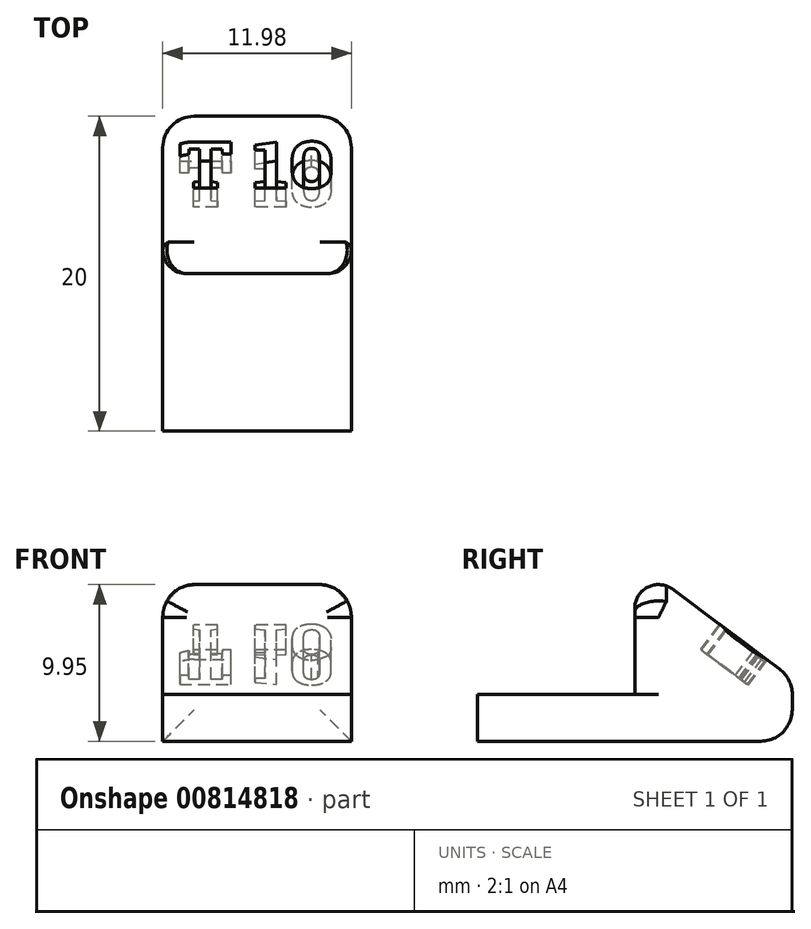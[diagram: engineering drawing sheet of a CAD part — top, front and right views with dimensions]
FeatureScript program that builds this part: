
annotation { "Feature Type Name" : "Feature", "Feature Type Description" : "" }
export const myFeature = defineFeature(function(context is Context, id is Id, definition is map)
    precondition{}
    {
        {
            var Q0;
            Q0=qCreatedBy(makeId("Top.planeOp"),FACE);
            var sketch = newSketch(context, id + "F0", { "sketchPlane" : qUnion([Q0])});
            skLineSegment(sketch, "E0.bottom", {"start": v(6, 10) * mm, "end": v(-5.99, 10) * mm});
            skLineSegment(sketch, "E0.top", {"start": v(6, -10) * mm, "end": v(-5.99, -10) * mm});
            skLineSegment(sketch, "E0.left", {"start": v(6, 10) * mm, "end": v(6, -10) * mm});
            skLineSegment(sketch, "E0.right", {"start": v(-5.99, 10) * mm, "end": v(-5.99, -10) * mm});
            skPoint(sketch, "E0.middle", {"position": v(0, 0) * mm});
            skSolve(sketch);
        }
        {
            var Q0;
            Q0 = qSketchRegion(id + "F0", true);
            extrude(context, id + "F1", {"entities" : qUnion([Q0]), "depth" : 2.98 * mm, "offsetDistance" : 25 * mm});
        }
        {
            var Q0;
            Q0=makeQuery(id+"F1.opExtrude","CAP_FACE",FACE,{"disambiguationData":[OSD([sQuery(id+"F0.wireOp",EDGE,"E0.bottom"),sQuery(id+"F0.wireOp",EDGE,"E0.top"),sQuery(id+"F0.wireOp",EDGE,"E0.left"),sQuery(id+"F0.wireOp",EDGE,"E0.right")])],"isStart":false});
            var sketch = newSketch(context, id + "F2", { "sketchPlane" : qUnion([Q0])});
            skLineSegment(sketch, "E1.bottom", {"start": v(-5.99, 10) * mm, "end": v(6, 10) * mm});
            skLineSegment(sketch, "E1.top", {"start": v(-5.99, 0) * mm, "end": v(6, 0) * mm});
            skLineSegment(sketch, "E1.left", {"start": v(-5.99, 10) * mm, "end": v(-5.99, 0) * mm});
            skLineSegment(sketch, "E1.right", {"start": v(6, 10) * mm, "end": v(6, 0) * mm});
            skSolve(sketch);
        }
        {
            var Q0;
            Q0=makeQuery(id+"F2.imprint","IMPRINT",FACE,{"disambiguationData":[TD([[makeQuery(id+"F2.imprint","IMPRINT",EDGE,{"derivedFrom":sQuery(id+"F2.wireOp",EDGE,"E1.bottom")}),1.0]])]});
            extrude(context, id + "F3", {"entities" : qUnion([Q0]), "operationType" : NewBodyOperationType.ADD, "depth" : 7 * mm, "offsetDistance" : 25 * mm});
        }
        {
            var Q0;
            Q0=makeQuery(id+"F3.opExtrude","CAP_EDGE",EDGE,{"disambiguationData":[OSD([sQuery(id+"F2.wireOp",EDGE,"E1.bottom")])],"isStart":false});
            chamfer(context, id + "F4", {"entities" : qUnion([Q0]), "chamferType" : ChamferType.TWO_OFFSETS, "width1" : 8 * mm, "oppositeDirection" : false, "width2" : 6 * mm, "tangentPropagation" : true});
        }
        {
            var Q0;
            Q0=makeQuery(id+"F4.opChamfer","BLEND_FACE",FACE,{"disambiguationData":[OSD([sQuery(id+"F2.wireOp",EDGE,"E1.bottom")])]});
            var sketch = newSketch(context, id + "F5", { "sketchPlane" : qUnion([Q0])});
            skText(sketch, "E2", { "text": "T 10", "fontName": "RobotoSlab-Bold.ttf"});
            const initialGuessF5  = {"E2": [-0.005, -8e-05, 1, 0, 0.0037]};
            skSetInitialGuess(sketch, initialGuessF5);
            skSolve(sketch);
        }
        {
            var Q0;
            Q0 = qSketchRegion(id + "F5", true);
            extrude(context, id + "F6", {"entities" : qUnion([Q0]), "operationType" : NewBodyOperationType.REMOVE, "oppositeDirection" : true, "depth" : 2 * mm, "offsetDistance" : 25 * mm});
        }
        {
            var Q0;
            {var subQ0=sQuery(id+"F2.wireOp",EDGE,"E1.bottom");Q0=makeQuery(id+"F4.opChamfer","BLEND_EDGE",EDGE,{"blendedFrom":[makeQuery(id+"F3.opExtrude","CAP_EDGE",EDGE,{"disambiguationData":[OSD([subQ0])],"isStart":false}),makeQuery(id+"F3.boolean.opBoolean","MERGE",FACE,{"derivedFrom":[makeQuery(id+"F1.opExtrude","SWEPT_FACE",FACE,{"disambiguationData":[OSD([sQuery(id+"F0.wireOp",EDGE,"E0.bottom")])]}),makeQuery(id+"F3.opExtrude","SWEPT_FACE",FACE,{"disambiguationData":[OSD([subQ0])]})]})],"blendedInto":[makeQuery(id+"F3.boolean.opBoolean","MERGE",FACE,{"derivedFrom":[makeQuery(id+"F1.opExtrude","SWEPT_FACE",FACE,{"disambiguationData":[OSD([sQuery(id+"F0.wireOp",EDGE,"E0.bottom")])]}),makeQuery(id+"F3.opExtrude","SWEPT_FACE",FACE,{"disambiguationData":[OSD([subQ0])]})]})]});}
            var Q1;
            {var subQ0=sQuery(id+"F2.wireOp",EDGE,"E1.bottom");Q1=makeQuery(id+"F4.opChamfer","BLEND_EDGE",EDGE,{"blendedFrom":[makeQuery(id+"F3.opExtrude","CAP_EDGE",EDGE,{"disambiguationData":[OSD([subQ0])],"isStart":false}),makeQuery(id+"F3.opExtrude","CAP_FACE",FACE,{"disambiguationData":[OSD([subQ0,sQuery(id+"F2.wireOp",EDGE,"E1.top"),sQuery(id+"F2.wireOp",EDGE,"E1.left"),sQuery(id+"F2.wireOp",EDGE,"E1.right")])],"isStart":false})],"blendedInto":[makeQuery(id+"F3.opExtrude","CAP_FACE",FACE,{"disambiguationData":[OSD([subQ0,sQuery(id+"F2.wireOp",EDGE,"E1.top"),sQuery(id+"F2.wireOp",EDGE,"E1.left"),sQuery(id+"F2.wireOp",EDGE,"E1.right")])],"isStart":false})]});}
            var Q2;
            Q2=makeQuery(id+"F4.opChamfer","BLEND_EDGE",EDGE,{"blendedFrom":[makeQuery(id+"F3.opExtrude","CAP_EDGE",EDGE,{"disambiguationData":[OSD([sQuery(id+"F2.wireOp",EDGE,"E1.bottom")])],"isStart":false}),makeQuery(id+"F3.boolean.opBoolean","MERGE",FACE,{"derivedFrom":[makeQuery(id+"F1.opExtrude","SWEPT_FACE",FACE,{"disambiguationData":[OSD([sQuery(id+"F0.wireOp",EDGE,"E0.left")])]}),makeQuery(id+"F3.opExtrude","SWEPT_FACE",FACE,{"disambiguationData":[OSD([sQuery(id+"F2.wireOp",EDGE,"E1.right")])]})]})],"blendedInto":[makeQuery(id+"F3.boolean.opBoolean","MERGE",FACE,{"derivedFrom":[makeQuery(id+"F1.opExtrude","SWEPT_FACE",FACE,{"disambiguationData":[OSD([sQuery(id+"F0.wireOp",EDGE,"E0.left")])]}),makeQuery(id+"F3.opExtrude","SWEPT_FACE",FACE,{"disambiguationData":[OSD([sQuery(id+"F2.wireOp",EDGE,"E1.right")])]})]})]});
            var Q3;
            Q3=makeQuery(id+"F4.opChamfer","BLEND_EDGE",EDGE,{"blendedFrom":[makeQuery(id+"F3.opExtrude","CAP_EDGE",EDGE,{"disambiguationData":[OSD([sQuery(id+"F2.wireOp",EDGE,"E1.bottom")])],"isStart":false}),makeQuery(id+"F3.boolean.opBoolean","MERGE",FACE,{"derivedFrom":[makeQuery(id+"F1.opExtrude","SWEPT_FACE",FACE,{"disambiguationData":[OSD([sQuery(id+"F0.wireOp",EDGE,"E0.right")])]}),makeQuery(id+"F3.opExtrude","SWEPT_FACE",FACE,{"disambiguationData":[OSD([sQuery(id+"F2.wireOp",EDGE,"E1.left")])]})]})],"blendedInto":[makeQuery(id+"F3.boolean.opBoolean","MERGE",FACE,{"derivedFrom":[makeQuery(id+"F1.opExtrude","SWEPT_FACE",FACE,{"disambiguationData":[OSD([sQuery(id+"F0.wireOp",EDGE,"E0.right")])]}),makeQuery(id+"F3.opExtrude","SWEPT_FACE",FACE,{"disambiguationData":[OSD([sQuery(id+"F2.wireOp",EDGE,"E1.left")])]})]})]});
            var Q4;
            Q4=makeQuery(id+"F3.boolean.opBoolean","MERGE",EDGE,{"derivedFrom":[makeQuery(id+"F1.opExtrude","SWEPT_EDGE",EDGE,{"disambiguationData":[OSD([sQuery(id+"F0.wireOp",EDGE,"E0.bottom"),sQuery(id+"F0.wireOp",EDGE,"E0.left")])]}),makeQuery(id+"F3.opExtrude","SWEPT_EDGE",EDGE,{"disambiguationData":[OSD([sQuery(id+"F2.wireOp",EDGE,"E1.bottom"),sQuery(id+"F2.wireOp",EDGE,"E1.right")])]})]});
            var Q5;
            Q5=makeQuery(id+"F3.boolean.opBoolean","MERGE",EDGE,{"derivedFrom":[makeQuery(id+"F1.opExtrude","SWEPT_EDGE",EDGE,{"disambiguationData":[OSD([sQuery(id+"F0.wireOp",EDGE,"E0.bottom"),sQuery(id+"F0.wireOp",EDGE,"E0.right")])]}),makeQuery(id+"F3.opExtrude","SWEPT_EDGE",EDGE,{"disambiguationData":[OSD([sQuery(id+"F2.wireOp",EDGE,"E1.bottom"),sQuery(id+"F2.wireOp",EDGE,"E1.left")])]})]});
            var Q6;
            Q6=makeQuery(id+"F3.opExtrude","CAP_EDGE",EDGE,{"disambiguationData":[OSD([sQuery(id+"F2.wireOp",EDGE,"E1.left")])],"isStart":false});
            var Q7;
            Q7=makeQuery(id+"F3.opExtrude","CAP_EDGE",EDGE,{"disambiguationData":[OSD([sQuery(id+"F2.wireOp",EDGE,"E1.right")])],"isStart":false});
            var Q8;
            Q8=makeQuery(id+"F1.opExtrude","CAP_EDGE",EDGE,{"disambiguationData":[OSD([sQuery(id+"F0.wireOp",EDGE,"E0.bottom")])],"isStart":true});
            fillet(context, id + "F7", {"entities" : qUnion([Q0, Q1, Q2, Q3, Q4, Q5, Q6, Q7, Q8]), "radius" : 2 * mm, "tangentPropagation" : true, "allowEdgeOverflow" : false});
        }
        {
            var Q0;
            Q0=makeQuery(id+"F3.opExtrude","CAP_EDGE",EDGE,{"disambiguationData":[OSD([sQuery(id+"F2.wireOp",EDGE,"E1.top")])],"isStart":false});
            fillet(context, id + "F8", {"entities" : qUnion([Q0]), "radius" : 1.5 * mm, "tangentPropagation" : true, "allowEdgeOverflow" : false});
        }
    });
